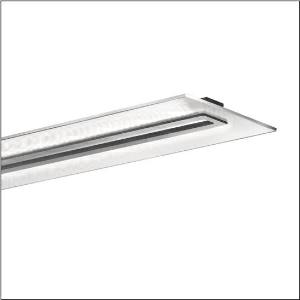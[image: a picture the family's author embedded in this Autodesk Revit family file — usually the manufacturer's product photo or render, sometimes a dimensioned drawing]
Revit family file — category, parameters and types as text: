
# Revit family: vega_r__11_5mn238dle0s_e1af
name_source: partatom
category: Lighting Fixtures
units: mm (PartAtom-declared; Revit-internal decimal feet)

## family parameters
Cut with Voids When Loaded = No
Host = Face
Light Source = No
Part Type = Normal
Room Calculation Point = No
Round Connector Dimension = Use Diameter
Shared = No

## types (1)
- --- (1 x LED 4000K / CRI = 80 (unbekannt), 8130 lm, 4000K)
    Apparent Load = 62 VA
    CIE Flux Codes = 61 86 97 62 100
    Color Rendering = 80
    Color Temperature = 4000K
    Default Elevation = 1800 mm
    Description = Vega® 11, office luminaire, primary light control with prismatic reflector, of PMMA, transparent prismatic structure, CAT 2 (L<= 1500cd/m²), light emission: direct/indirect distribution, primary light characteristic: symmetric, installation type: suspended mounting, surface-mounted, LED, rated luminous flux: 8.130lm, luminous efficacy: 131lm/W, light colour: 840, colour temperature: 4000K, control gear: ECG, with terminal, 3+2-pole, max. 2.5mm², mains connection: 230V, AC, 50Hz, connection cable inclusive, cable length: 1,5m, rated input power: 62W, luminaire housing, rectangular, rounded, of aluminium section, anodised, metallic grey (RAL 9006), length: 1.250mm, width: 350mm, height: 43mm, luminaire housing, lower part, of aluminium section, anodised, metallic grey (RAL 9006), of PC, grey, protection rating (complete): IP20, insulation class (complete): insulation class I (protective earthing), certification: CE, permissible operating ambient temperature: 0..+35°C, standard: EN 50419, packaging unit: 1 piece
    Height = 40 mm  [stored 0.131234 ft]
    Lamp = 1 x LED 4000K / CRI >= 80 (unbekannt)
    Lamp Light Flux = 8130 lm
    Lamp count = 1
    Length = 1250 mm
    Luminous efficacy = 131 lm/W
    Manufacturer = Siteco
    ModVariant = No
    Model = 5MN238DLE0S
    Mounting Place = Ceiling
    Mounting Type = Pendant
    Number of Poles = 1
    OnlyDefault = Yes
    Power Factor = 1
    Product Name = Vega® 11
    Product group = office luminaire | ceiling pendant
    ProductGroupID = 902
    Protection Class = Protection class I
    Protection Degree = IP 20
    RLX_Detail_Level = 1
    RLX_Emergency_Light_Flux = 0 lm
    RLX_Emergency_Type = 0
    RLX_Emergency_Type_DB = No
    RlxData = <blob elided: 63069 chars, md5=5161c794>
    Socket = socket
    Standby Power = 0 W
    System Light Flux = 8130 lm
    System Power = 62 W
    Type Comments = factory setting: luminous flux: 100 % | dim-lin: 254 | 458 mA
    Type Image = l_1004807.jpg
    URL = http://relux.com
    VarID = @adj_165581
    Voltage = 0 V
    Weight = 0.00 kg
    Width = 350 mm

note: [stored X ft] marks values corroborated as IEEE doubles in the binary element streams (Revit-internal decimal feet)

## geometry (parser evidence)
native form markers: Blend x4, Sweep x12
no freeform markers — native parametric forms only
